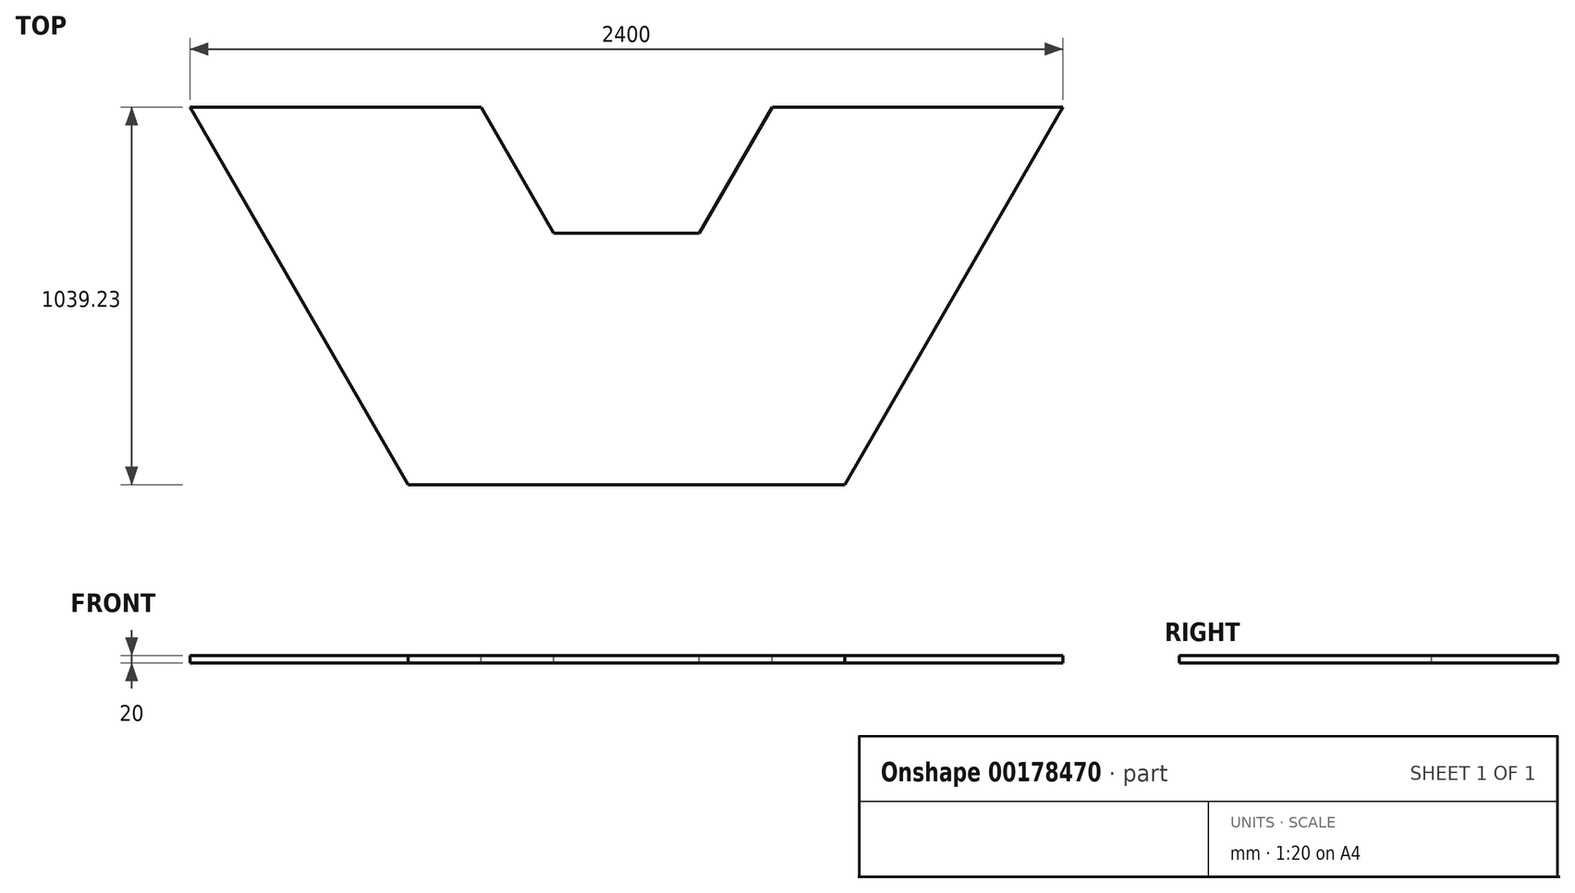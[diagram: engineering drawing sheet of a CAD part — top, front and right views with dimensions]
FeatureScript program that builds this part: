
annotation { "Feature Type Name" : "Feature", "Feature Type Description" : "" }
export const myFeature = defineFeature(function(context is Context, id is Id, definition is map)
    precondition{}
    {
        {
            var Q0;
            Q0=qCreatedBy(makeId("Top.planeOp"),FACE);
            cPlane(context, id + "F0", {"entities" : qUnion([Q0]), "cplaneType" : CPlaneType.OFFSET, "offset" : 800 * mm, "width" : 152.4 * mm, "height" : 152.4 * mm});
        }
        {
            var Q0;
            Q0=qCreatedBy(id+"F0.planeOp",FACE);
            var sketch = newSketch(context, id + "F1", { "sketchPlane" : qUnion([Q0])});
            skLineSegment(sketch, "E0", {"start": v(0, 0) * mm, "end": v(200, 346.41) * mm});
            skLineSegment(sketch, "E1", {"start": v(200, 346.41) * mm, "end": v(-200, 346.41) * mm});
            skLineSegment(sketch, "E2", {"start": v(-200, 346.41) * mm, "end": v(0, 0) * mm});
            skLineSegment(sketch, "E3", {"start": v(200, 346.41) * mm, "end": v(400, 0) * mm});
            skLineSegment(sketch, "E4", {"start": v(400, 0) * mm, "end": v(0, 0) * mm});
            skLineSegment(sketch, "E5", {"start": v(-400, 0) * mm, "end": v(-200, 346.41) * mm});
            skLineSegment(sketch, "E6", {"start": v(200, 346.41) * mm, "end": v(400, 692.82) * mm});
            skLineSegment(sketch, "E7", {"start": v(400, 692.82) * mm, "end": v(600, 346.41) * mm});
            skLineSegment(sketch, "E8", {"start": v(600, 346.41) * mm, "end": v(400, 0) * mm});
            skLineSegment(sketch, "E9", {"start": v(200, 346.41) * mm, "end": v(600, 346.41) * mm});
            skLineSegment(sketch, "E10", {"start": v(600, 346.41) * mm, "end": v(800, 0) * mm});
            skLineSegment(sketch, "E11", {"start": v(800, 0) * mm, "end": v(400, 0) * mm});
            skLineSegment(sketch, "E12", {"start": v(600, -346.41) * mm, "end": v(800, 0) * mm});
            skLineSegment(sketch, "E13", {"start": v(600, -346.41) * mm, "end": v(400, 0) * mm});
            skLineSegment(sketch, "E14", {"start": v(400, 692.82) * mm, "end": v(800, 692.82) * mm});
            skLineSegment(sketch, "E15", {"start": v(800, 692.82) * mm, "end": v(600, 346.41) * mm});
            skLineSegment(sketch, "E16", {"start": v(1000, 346.41) * mm, "end": v(800, 692.82) * mm});
            skLineSegment(sketch, "E17", {"start": v(600, 346.41) * mm, "end": v(1000, 346.41) * mm});
            skLineSegment(sketch, "E18", {"start": v(800, 0) * mm, "end": v(1000, 346.41) * mm});
            skLineSegment(sketch, "E19", {"start": v(600, -346.41) * mm, "end": v(200, -346.41) * mm});
            skLineSegment(sketch, "E20", {"start": v(200, -346.41) * mm, "end": v(400, 0) * mm});
            skLineSegment(sketch, "E21", {"start": v(0, 0) * mm, "end": v(200, -346.41) * mm});
            skLineSegment(sketch, "E22", {"start": v(-200, -346.41) * mm, "end": v(0, 0) * mm});
            skLineSegment(sketch, "E23", {"start": v(-400, 0) * mm, "end": v(0, 0) * mm});
            skLineSegment(sketch, "E24", {"start": v(-400, 0) * mm, "end": v(-200, -346.41) * mm});
            skLineSegment(sketch, "E25", {"start": v(200, -346.41) * mm, "end": v(-200, -346.41) * mm});
            skLineSegment(sketch, "E26", {"start": v(-600, -346.41) * mm, "end": v(-400, 0) * mm});
            skLineSegment(sketch, "E27", {"start": v(-200, -346.41) * mm, "end": v(-600, -346.41) * mm});
            skLineSegment(sketch, "E28", {"start": v(-800, 0) * mm, "end": v(-600, -346.41) * mm});
            skLineSegment(sketch, "E29", {"start": v(-800, 0) * mm, "end": v(-400, 0) * mm});
            skLineSegment(sketch, "E30", {"start": v(-600, 346.41) * mm, "end": v(-400, 0) * mm});
            skLineSegment(sketch, "E31", {"start": v(-600, 346.41) * mm, "end": v(-200, 346.41) * mm});
            skLineSegment(sketch, "E32", {"start": v(-200, 346.41) * mm, "end": v(-400, 692.82) * mm});
            skLineSegment(sketch, "E33", {"start": v(-400, 692.82) * mm, "end": v(-600, 346.41) * mm});
            skLineSegment(sketch, "E34", {"start": v(-800, 0) * mm, "end": v(-600, 346.41) * mm});
            skLineSegment(sketch, "E35", {"start": v(-400, 692.82) * mm, "end": v(-800, 692.82) * mm});
            skLineSegment(sketch, "E36", {"start": v(-800, 692.82) * mm, "end": v(-600, 346.41) * mm});
            skLineSegment(sketch, "E37", {"start": v(-800, 692.82) * mm, "end": v(-1000, 346.41) * mm});
            skLineSegment(sketch, "E38", {"start": v(-1000, 346.41) * mm, "end": v(-800, 0) * mm});
            skLineSegment(sketch, "E39", {"start": v(-600, 346.41) * mm, "end": v(-1000, 346.41) * mm});
            skLineSegment(sketch, "E40", {"start": v(-1000, 346.41) * mm, "end": v(-1200, 692.82) * mm});
            skLineSegment(sketch, "E41", {"start": v(-1200, 692.82) * mm, "end": v(-800, 692.82) * mm});
            skLineSegment(sketch, "E42", {"start": v(800, 692.82) * mm, "end": v(1200, 692.82) * mm});
            skLineSegment(sketch, "E43", {"start": v(1200, 692.82) * mm, "end": v(1000, 346.41) * mm});
            skSolve(sketch);
        }
        {
            var Q0;
            Q0=makeQuery(id+"F1.imprint","IMPRINT",FACE,{"disambiguationData":[TD([[makeQuery(id+"F1.imprint","IMPRINT",EDGE,{"derivedFrom":sQuery(id+"F1.wireOp",EDGE,"E0")}),1.0]])]});
            var Q1;
            Q1=makeQuery(id+"F1.imprint","IMPRINT",FACE,{"disambiguationData":[TD([[makeQuery(id+"F1.imprint","IMPRINT",EDGE,{"derivedFrom":sQuery(id+"F1.wireOp",EDGE,"E36")}),-1.0]])]});
            var Q2;
            Q2=makeQuery(id+"F1.imprint","IMPRINT",FACE,{"disambiguationData":[TD([[makeQuery(id+"F1.imprint","IMPRINT",EDGE,{"derivedFrom":sQuery(id+"F1.wireOp",EDGE,"E0")}),-1.0]])]});
            var Q3;
            Q3=makeQuery(id+"F1.imprint","IMPRINT",FACE,{"disambiguationData":[TD([[makeQuery(id+"F1.imprint","IMPRINT",EDGE,{"derivedFrom":sQuery(id+"F1.wireOp",EDGE,"E22")}),1.0]])]});
            var Q4;
            Q4=makeQuery(id+"F1.imprint","IMPRINT",FACE,{"disambiguationData":[TD([[makeQuery(id+"F1.imprint","IMPRINT",EDGE,{"derivedFrom":sQuery(id+"F1.wireOp",EDGE,"E34")}),1.0]])]});
            var Q5;
            Q5=makeQuery(id+"F1.imprint","IMPRINT",FACE,{"disambiguationData":[TD([[makeQuery(id+"F1.imprint","IMPRINT",EDGE,{"derivedFrom":sQuery(id+"F1.wireOp",EDGE,"E16")}),-1.0]])]});
            var Q6;
            Q6=makeQuery(id+"F1.imprint","IMPRINT",FACE,{"disambiguationData":[TD([[makeQuery(id+"F1.imprint","IMPRINT",EDGE,{"derivedFrom":sQuery(id+"F1.wireOp",EDGE,"E2")}),-1.0]])]});
            var Q7;
            Q7=makeQuery(id+"F1.imprint","IMPRINT",FACE,{"disambiguationData":[TD([[makeQuery(id+"F1.imprint","IMPRINT",EDGE,{"derivedFrom":sQuery(id+"F1.wireOp",EDGE,"E37")}),-1.0]])]});
            var Q8;
            Q8=makeQuery(id+"F1.imprint","IMPRINT",FACE,{"disambiguationData":[TD([[makeQuery(id+"F1.imprint","IMPRINT",EDGE,{"derivedFrom":sQuery(id+"F1.wireOp",EDGE,"E6")}),-1.0]])]});
            var Q9;
            Q9=makeQuery(id+"F1.imprint","IMPRINT",FACE,{"disambiguationData":[TD([[makeQuery(id+"F1.imprint","IMPRINT",EDGE,{"derivedFrom":sQuery(id+"F1.wireOp",EDGE,"E7")}),1.0]])]});
            var Q10;
            Q10=makeQuery(id+"F1.imprint","IMPRINT",FACE,{"disambiguationData":[TD([[makeQuery(id+"F1.imprint","IMPRINT",EDGE,{"derivedFrom":sQuery(id+"F1.wireOp",EDGE,"E10")}),1.0]])]});
            var Q11;
            Q11=makeQuery(id+"F1.imprint","IMPRINT",FACE,{"disambiguationData":[TD([[makeQuery(id+"F1.imprint","IMPRINT",EDGE,{"derivedFrom":sQuery(id+"F1.wireOp",EDGE,"E4")}),1.0]])]});
            var Q12;
            Q12=makeQuery(id+"F1.imprint","IMPRINT",FACE,{"disambiguationData":[TD([[makeQuery(id+"F1.imprint","IMPRINT",EDGE,{"derivedFrom":sQuery(id+"F1.wireOp",EDGE,"E21")}),-1.0]])]});
            var Q13;
            Q13=makeQuery(id+"F1.imprint","IMPRINT",FACE,{"disambiguationData":[TD([[makeQuery(id+"F1.imprint","IMPRINT",EDGE,{"derivedFrom":sQuery(id+"F1.wireOp",EDGE,"E11")}),1.0]])]});
            var Q14;
            Q14=makeQuery(id+"F1.imprint","IMPRINT",FACE,{"disambiguationData":[TD([[makeQuery(id+"F1.imprint","IMPRINT",EDGE,{"derivedFrom":sQuery(id+"F1.wireOp",EDGE,"E13")}),1.0]])]});
            var Q15;
            Q15=makeQuery(id+"F1.imprint","IMPRINT",FACE,{"disambiguationData":[TD([[makeQuery(id+"F1.imprint","IMPRINT",EDGE,{"derivedFrom":sQuery(id+"F1.wireOp",EDGE,"E33")}),-1.0]])]});
            var Q16;
            Q16=makeQuery(id+"F1.imprint","IMPRINT",FACE,{"disambiguationData":[TD([[makeQuery(id+"F1.imprint","IMPRINT",EDGE,{"derivedFrom":sQuery(id+"F1.wireOp",EDGE,"E24")}),-1.0]])]});
            var Q17;
            Q17=makeQuery(id+"F1.imprint","IMPRINT",FACE,{"disambiguationData":[TD([[makeQuery(id+"F1.imprint","IMPRINT",EDGE,{"derivedFrom":sQuery(id+"F1.wireOp",EDGE,"E26")}),1.0]])]});
            var Q18;
            Q18=makeQuery(id+"F1.imprint","IMPRINT",FACE,{"disambiguationData":[TD([[makeQuery(id+"F1.imprint","IMPRINT",EDGE,{"derivedFrom":sQuery(id+"F1.wireOp",EDGE,"E31")}),1.0]])]});
            var Q19;
            Q19=makeQuery(id+"F1.imprint","IMPRINT",FACE,{"disambiguationData":[TD([[makeQuery(id+"F1.imprint","IMPRINT",EDGE,{"derivedFrom":sQuery(id+"F1.wireOp",EDGE,"E5")}),1.0]])]});
            var Q20;
            Q20=makeQuery(id+"F1.imprint","IMPRINT",FACE,{"disambiguationData":[TD([[makeQuery(id+"F1.imprint","IMPRINT",EDGE,{"derivedFrom":sQuery(id+"F1.wireOp",EDGE,"E3")}),1.0]])]});
            var Q21;
            Q21=makeQuery(id+"F1.imprint","IMPRINT",FACE,{"disambiguationData":[TD([[makeQuery(id+"F1.imprint","IMPRINT",EDGE,{"derivedFrom":sQuery(id+"F1.wireOp",EDGE,"E15")}),1.0]])]});
            var Q22;
            Q22=makeQuery(id+"F1.imprint","IMPRINT",FACE,{"disambiguationData":[TD([[makeQuery(id+"F1.imprint","IMPRINT",EDGE,{"derivedFrom":sQuery(id+"F1.wireOp",EDGE,"E29")}),1.0]])]});
            var Q23;
            Q23=makeQuery(id+"F1.imprint","IMPRINT",FACE,{"disambiguationData":[TD([[makeQuery(id+"F1.imprint","IMPRINT",EDGE,{"derivedFrom":sQuery(id+"F1.wireOp",EDGE,"E8")}),1.0]])]});
            extrude(context, id + "F2", {"entities" : qUnion([Q0, Q1, Q2, Q3, Q4, Q5, Q6, Q7, Q8, Q9, Q10, Q11, Q12, Q13, Q14, Q15, Q16, Q17, Q18, Q19, Q20, Q21, Q22, Q23]), "oppositeDirection" : true, "depth" : 20 * mm});
        }
    });
